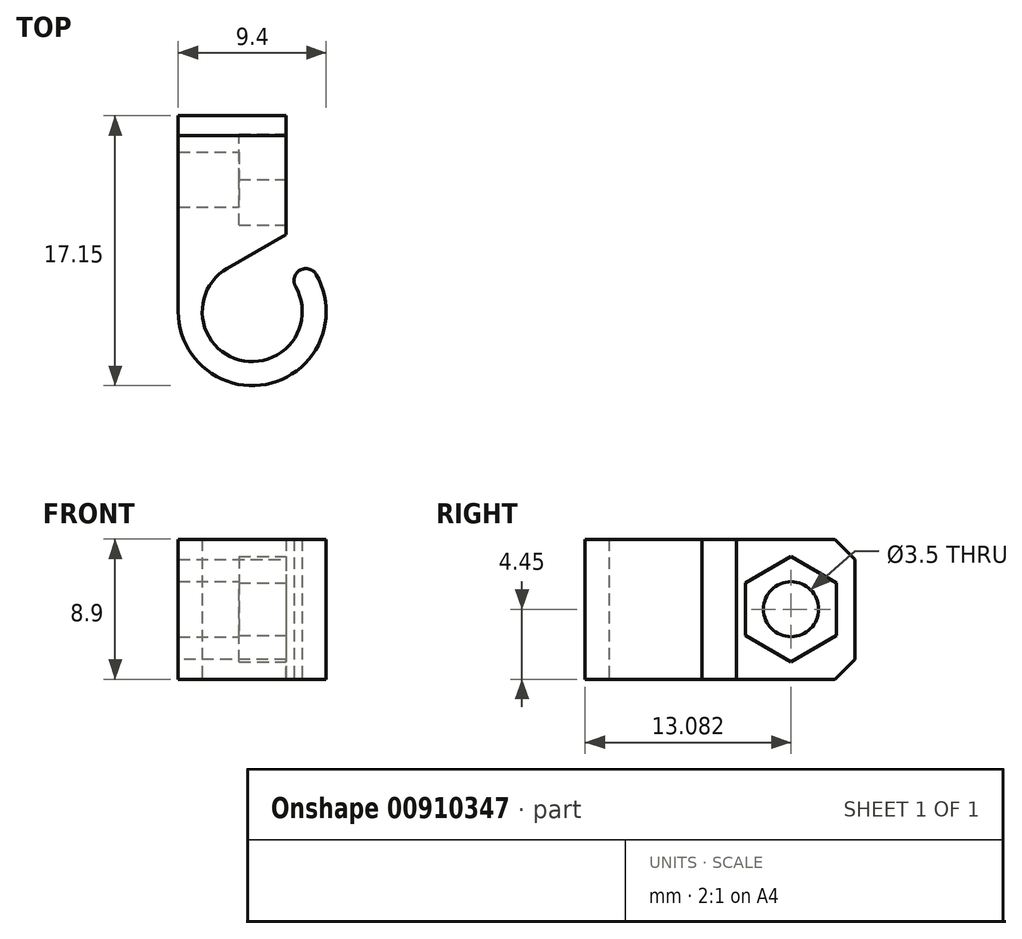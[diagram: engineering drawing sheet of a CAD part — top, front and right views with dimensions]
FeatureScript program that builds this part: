
annotation { "Feature Type Name" : "Feature", "Feature Type Description" : "" }
export const myFeature = defineFeature(function(context is Context, id is Id, definition is map)
    precondition{}
    {
        {
            var Q0;
            Q0=qCreatedBy(makeId("Top.planeOp"),FACE);
            var sketch = newSketch(context, id + "F0", { "sketchPlane" : qUnion([Q0])});
            skLineSegment(sketch, "E0", {"start": v(-4.7, 12.45) * mm, "end": v(2.16, 12.45) * mm});
            skLineSegment(sketch, "E1", {"start": v(2.16, 12.45) * mm, "end": v(2.16, 4.91) * mm});
            skLineSegment(sketch, "E2", {"start": v(-4.7, 12.45) * mm, "end": v(-4.7, 0) * mm});
            skArc(sketch, "E3", {"start": v(-4.7, 0) * mm, "mid": v(1.22, -4.54) * mm, "end": v(4.07, 2.35) * mm});
            skArc(sketch, "E4", {"start": v(-1.59, 2.75) * mm, "mid": v(-0.82, -3.07) * mm, "end": v(2.75, 1.59) * mm});
            skArc(sketch, "E5", {"start": v(4.07, 2.35) * mm, "mid": v(3.03, 2.63) * mm, "end": v(2.75, 1.59) * mm});
            skLineSegment(sketch, "E6", {"start": v(-1.59, 2.75) * mm, "end": v(2.16, 4.91) * mm});
            skLineSegment(sketch, "E7", {"start": v(0, 0) * mm, "end": v(3.4, 1.97) * mm, "construction": true});
            skLineSegment(sketch, "E8", {"start": v(2.16, 11.28) * mm, "end": v(-0.84, 11.28) * mm, "construction": true});
            skLineSegment(sketch, "E9", {"start": v(-0.84, 5.49) * mm, "end": v(3.15, 5.49) * mm, "construction": true});
            skLineSegment(sketch, "E10", {"start": v(-0.84, 10.13) * mm, "end": v(-4.7, 10.13) * mm, "construction": true});
            skLineSegment(sketch, "E11", {"start": v(-0.84, 6.63) * mm, "end": v(-4.7, 6.63) * mm, "construction": true});
            skLineSegment(sketch, "E12", {"start": v(-0.84, 10.13) * mm, "end": v(-0.84, 8.38) * mm, "construction": true});
            skLineSegment(sketch, "E13", {"start": v(-0.84, 8.38) * mm, "end": v(-0.84, 6.63) * mm, "construction": true});
            skLineSegment(sketch, "E14", {"start": v(-0.84, 11.28) * mm, "end": v(-0.84, 5.49) * mm, "construction": true});
            skLineSegment(sketch, "E15", {"start": v(-0.84, 8.38) * mm, "end": v(2.16, 8.38) * mm, "construction": true});
            skSolve(sketch);
        }
        {
            var Q0;
            Q0 = qSketchRegion(id + "F0", true);
            extrude(context, id + "F1", {"entities" : qUnion([Q0]), "depth" : 8.9 * mm, "offsetDistance" : 25.4 * mm, "symmetric" : true});
        }
        {
            var Q0;
            Q0=makeQuery(id+"F1.opExtrude","SWEPT_FACE",FACE,{"disambiguationData":[OSD([sQuery(id+"F0.wireOp",EDGE,"E1")])]});
            var sketch = newSketch(context, id + "F2", { "sketchPlane" : qUnion([Q0])});
            skCircle(sketch, "E16", {"center": v(8.38, 0) * mm, "radius": 1.75 * mm});
            skLineSegment(sketch, "E17", {"start": v(8.68, 4.45) * mm, "end": v(8.38, 0) * mm, "construction": true});
            skLineSegment(sketch, "E18", {"start": v(12.45, 0) * mm, "end": v(8.38, 0) * mm, "construction": true});
            skSolve(sketch);
        }
        {
            var Q0;
            Q0 = qSketchRegion(id + "F2", true);
            extrude(context, id + "F3", {"entities" : qUnion([Q0]), "operationType" : NewBodyOperationType.REMOVE, "endBound" : BoundingType.THROUGH_ALL, "oppositeDirection" : true, "depth" : 25.4 * mm, "offsetDistance" : 25.4 * mm});
        }
        {
            var Q0;
            Q0=makeQuery(id+"F1.opExtrude","SWEPT_FACE",FACE,{"disambiguationData":[OSD([sQuery(id+"F0.wireOp",EDGE,"E1")])]});
            var sketch = newSketch(context, id + "F4", { "sketchPlane" : qUnion([Q0])});
            skCircle(sketch, "E19.cCircle", {"center": v(8.38, 0) * mm, "radius": 2.9 * mm, "construction": true});
            skLineSegment(sketch, "E19.0", {"start": v(11.28, 1.67) * mm, "end": v(11.28, -1.67) * mm});
            skLineSegment(sketch, "E19.1", {"start": v(11.28, -1.67) * mm, "end": v(8.38, -3.34) * mm});
            skLineSegment(sketch, "E19.2", {"start": v(8.38, -3.34) * mm, "end": v(5.49, -1.67) * mm});
            skLineSegment(sketch, "E19.3", {"start": v(5.49, -1.67) * mm, "end": v(5.49, 1.67) * mm});
            skLineSegment(sketch, "E19.4", {"start": v(5.49, 1.67) * mm, "end": v(8.38, 3.34) * mm});
            skLineSegment(sketch, "E19.5", {"start": v(8.38, 3.34) * mm, "end": v(11.28, 1.67) * mm});
            skPoint(sketch, "E19.0.midPoint", {"position": v(11.28, 0) * mm});
            skSolve(sketch);
        }
        {
            var Q0;
            Q0 = qSketchRegion(id + "F4", true);
            extrude(context, id + "F5", {"entities" : qUnion([Q0]), "operationType" : NewBodyOperationType.REMOVE, "oppositeDirection" : true, "depth" : 3 * mm, "offsetDistance" : 25.4 * mm});
        }
        {
            var Q0;
            Q0=makeQuery(id+"F1.opExtrude","CAP_EDGE",EDGE,{"disambiguationData":[OSD([sQuery(id+"F0.wireOp",EDGE,"E0")])],"isStart":true});
            var Q1;
            Q1=makeQuery(id+"F1.opExtrude","CAP_EDGE",EDGE,{"disambiguationData":[OSD([sQuery(id+"F0.wireOp",EDGE,"E0")])],"isStart":false});
            chamfer(context, id + "F6", {"entities" : qUnion([Q0, Q1]), "width" : 1.27 * mm, "tangentPropagation" : true});
        }
    });
